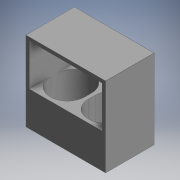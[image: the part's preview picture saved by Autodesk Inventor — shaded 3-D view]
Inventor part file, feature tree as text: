
AUTODESK INVENTOR PART (.ipt)
format: ipt  version: 2018 (Build 220112000, 112)  size: 142,336 bytes
history: native  units: in
note: dims shown in document units (in); Inventor stores cm internally (conversion verified against a paired STEP export)
features: extrude x3, other x2, pattern_linear x1, projected_geometry x1
ambient origin geometry x8: Origin, YZ Plane, XZ Plane, XY Plane, X Axis, Y Axis, Z Axis, Center Point
bodies: Solid1 (feature_tree)
feature tree (7):
  other  "Base Sketch"
  extrude  "Walls"  Depth=0.5512in TaperAngle=0.0deg
  extrude  "Back"  Depth=0.0394in
  extrude  "Whistle Hole"  Depth=0.0394in
  pattern_linear  "Rectangular Pattern2"  Spacing1=0.0394in  [1 undecoded]
  other  "Whistle Hole Sketch"
  projected_geometry  "Projected Loop1"
note: 1 required parameter value undecoded (feature->parameter linkage not recoverable at this tier; creation-order binding heuristic only, values carry confidence <= 0.55)
